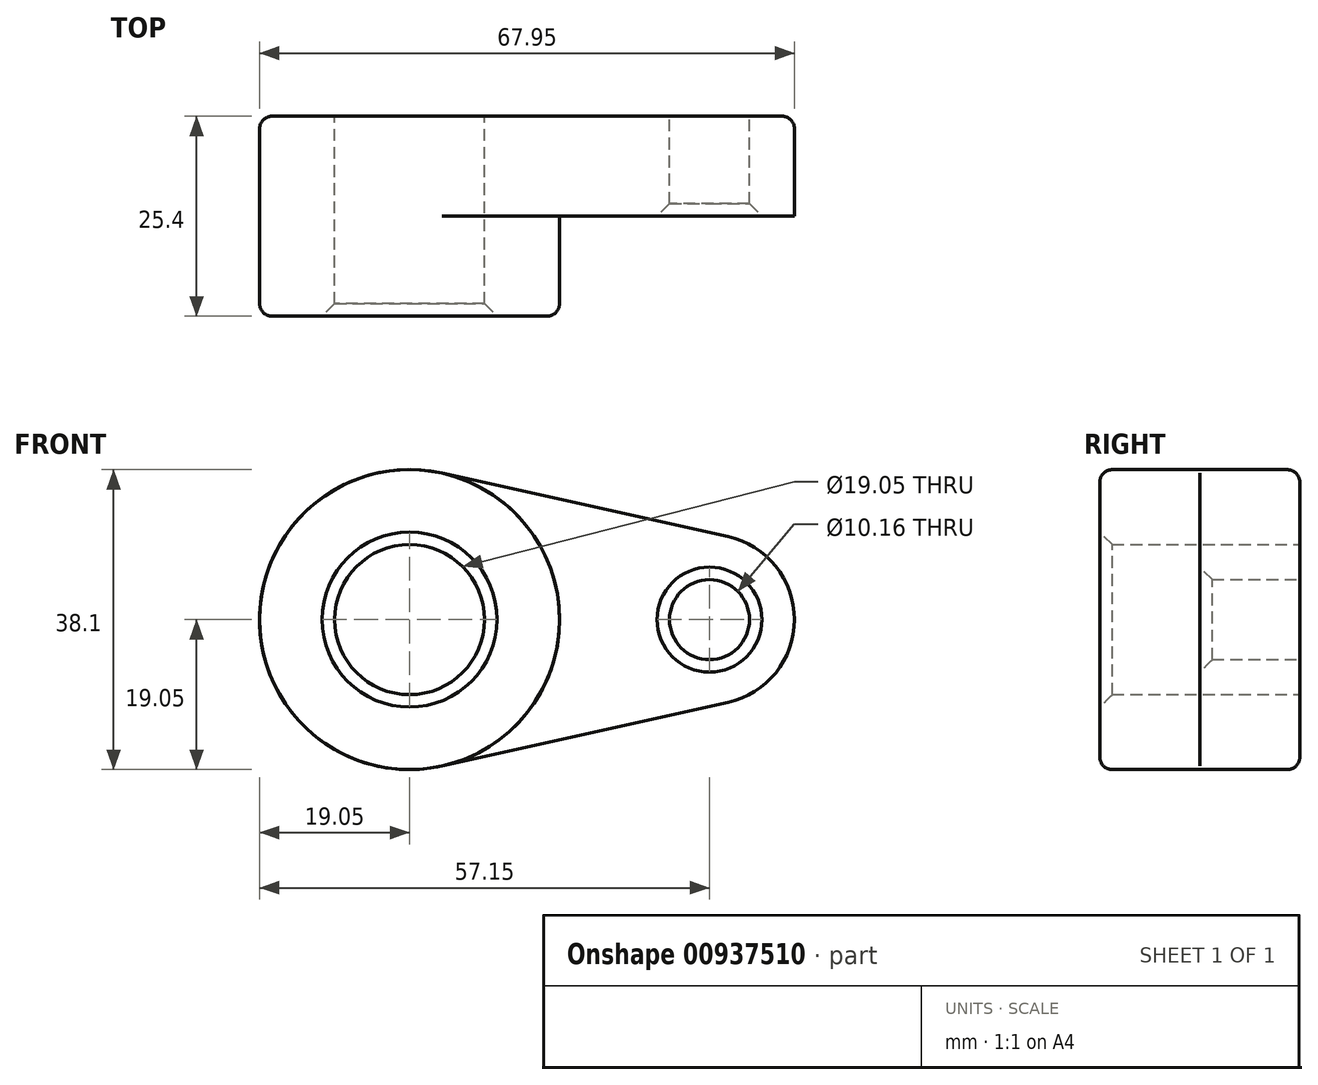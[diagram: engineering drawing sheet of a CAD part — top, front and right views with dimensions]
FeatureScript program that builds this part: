
annotation { "Feature Type Name" : "Feature", "Feature Type Description" : "" }
export const myFeature = defineFeature(function(context is Context, id is Id, definition is map)
    precondition{}
    {
        {
            var Q0;
            Q0=qCreatedBy(makeId("Front.planeOp"),FACE);
            var sketch = newSketch(context, id + "F0", { "sketchPlane" : qUnion([Q0])});
            skCircle(sketch, "E0", {"center": v(0, 0) * mm, "radius": 19.05 * mm});
            skCircle(sketch, "E1", {"center": v(38.1, 0) * mm, "radius": 10.8 * mm});
            skLineSegment(sketch, "E2", {"start": v(4.13, 18.6) * mm, "end": v(40.44, 10.54) * mm});
            skLineSegment(sketch, "E3", {"start": v(4.13, -18.6) * mm, "end": v(40.44, -10.54) * mm});
            skCircle(sketch, "E4", {"center": v(0, 0) * mm, "radius": 9.53 * mm});
            skCircle(sketch, "E5", {"center": v(38.1, 0) * mm, "radius": 5.08 * mm});
            skSolve(sketch);
        }
        {
            var Q0;
            Q0 = qSketchRegion(id + "F0", true);
            extrude(context, id + "F1", {"entities" : qUnion([Q0]), "depth" : 12.7 * mm, "offsetDistance" : 25.4 * mm});
        }
        {
            var Q0;
            Q0=makeQuery(id+"F0.imprint","IMPRINT",FACE,{"disambiguationData":[TD([[makeQuery(id+"F0.imprint","IMPRINT",EDGE,{"derivedFrom":sQuery(id+"F0.wireOp",EDGE,"E4")}),-1.0]])]});
            extrude(context, id + "F2", {"entities" : qUnion([Q0]), "operationType" : NewBodyOperationType.ADD, "depth" : 25.4 * mm, "offsetDistance" : 25.4 * mm});
        }
        {
            var Q0;
            Q0=makeQuery(id+"F2.opExtrude","CAP_EDGE",EDGE,{"disambiguationData":[OSD([sQuery(id+"F0.wireOp",EDGE,"E0")])],"isStart":false});
            var Q1;
            Q1=makeQuery(id+"F1.opExtrude","CAP_EDGE",EDGE,{"disambiguationData":[OSD([sQuery(id+"F0.wireOp",EDGE,"E0")])],"isStart":true});
            var Q2;
            Q2=makeQuery(id+"F1.opExtrude","CAP_EDGE",EDGE,{"disambiguationData":[OSD([sQuery(id+"F0.wireOp",EDGE,"E2")])],"isStart":true});
            var Q3;
            Q3=makeQuery(id+"F1.opExtrude","CAP_EDGE",EDGE,{"disambiguationData":[OSD([sQuery(id+"F0.wireOp",EDGE,"E1")])],"isStart":true});
            var Q4;
            Q4=makeQuery(id+"F1.opExtrude","CAP_EDGE",EDGE,{"disambiguationData":[OSD([sQuery(id+"F0.wireOp",EDGE,"E3")])],"isStart":true});
            fillet(context, id + "F3", {"entities" : qUnion([Q0, Q1, Q2, Q3, Q4]), "radius" : 1.59 * mm, "tangentPropagation" : true, "allowEdgeOverflow" : false});
        }
        {
            var Q0;
            Q0=makeQuery(id+"F2.opExtrude","CAP_EDGE",EDGE,{"disambiguationData":[OSD([sQuery(id+"F0.wireOp",EDGE,"E4")])],"isStart":false});
            var Q1;
            Q1=makeQuery(id+"F1.opExtrude","CAP_EDGE",EDGE,{"disambiguationData":[OSD([sQuery(id+"F0.wireOp",EDGE,"E5")])],"isStart":false});
            chamfer(context, id + "F4", {"entities" : qUnion([Q0, Q1]), "width" : 1.59 * mm, "tangentPropagation" : true});
        }
    });
